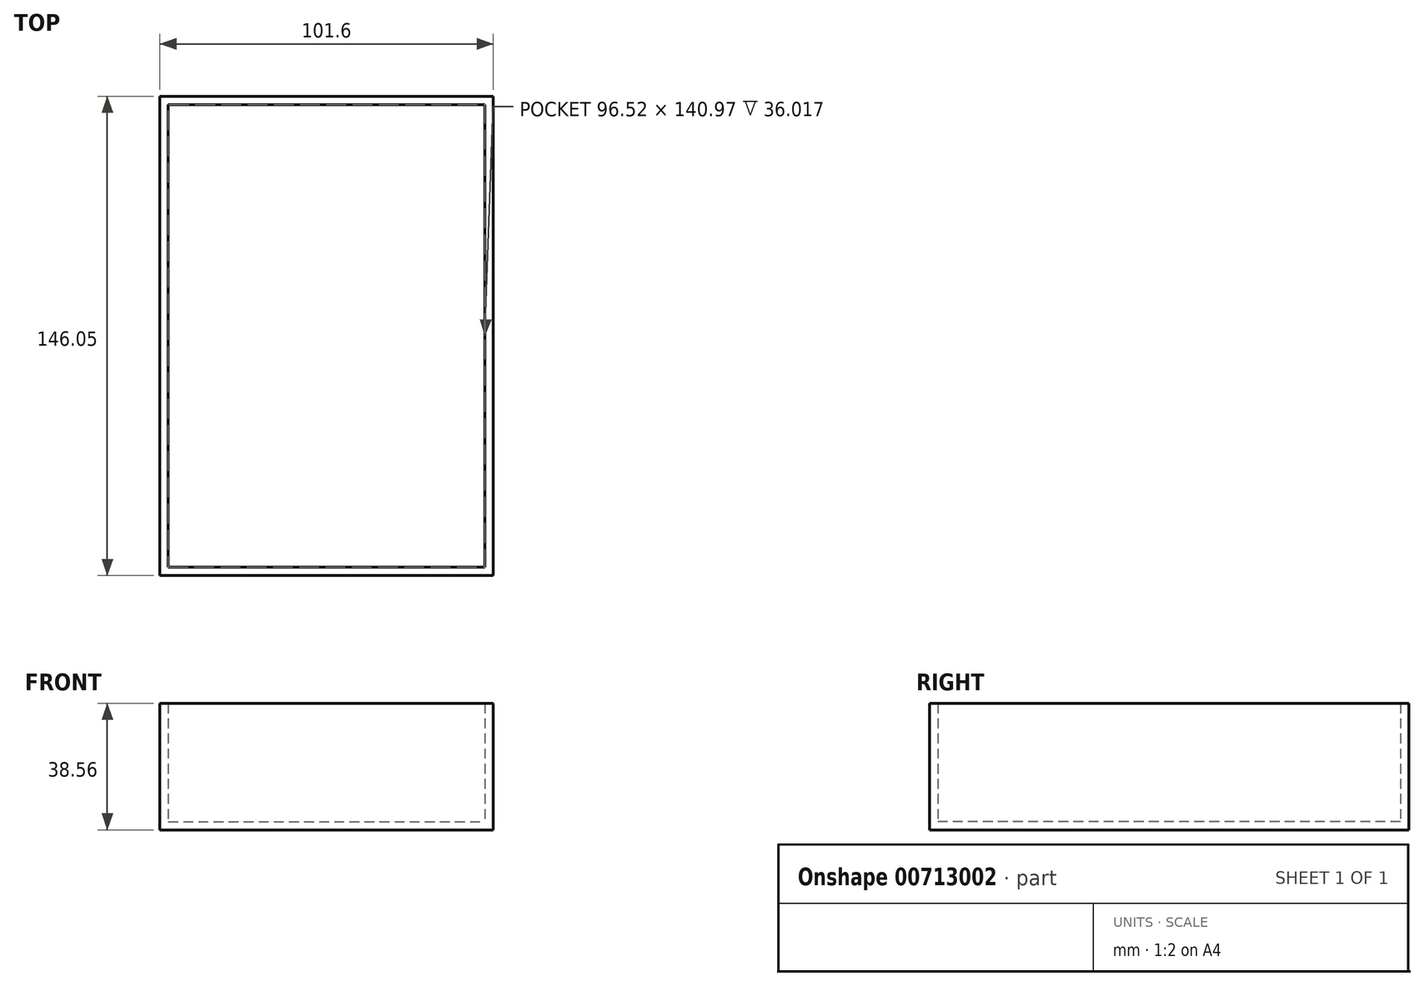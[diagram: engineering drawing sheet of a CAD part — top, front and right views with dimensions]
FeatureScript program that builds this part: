
annotation { "Feature Type Name" : "Feature", "Feature Type Description" : "" }
export const myFeature = defineFeature(function(context is Context, id is Id, definition is map)
    precondition{}
    {
        {
            var Q0;
            Q0=qCreatedBy(makeId("Top.planeOp"),FACE);
            var sketch = newSketch(context, id + "F0", { "sketchPlane" : qUnion([Q0])});
            skLineSegment(sketch, "E0.bottom", {"start": v(-59.18, 63.8) * mm, "end": v(42.42, 63.8) * mm});
            skLineSegment(sketch, "E0.top", {"start": v(-59.18, -82.24) * mm, "end": v(42.42, -82.24) * mm});
            skLineSegment(sketch, "E0.left", {"start": v(-59.18, 63.8) * mm, "end": v(-59.18, -82.24) * mm});
            skLineSegment(sketch, "E0.right", {"start": v(42.42, 63.8) * mm, "end": v(42.42, -82.24) * mm});
            skSolve(sketch);
        }
        {
            var Q0;
            Q0 = qSketchRegion(id + "F0", true);
            extrude(context, id + "F1", {"entities" : qUnion([Q0]), "depth" : 25.4 * mm, "offsetDistance" : 25.4 * mm});
        }
        {
            var Q0;
            Q0=makeQuery(id+"F1.opExtrude","CAP_FACE",FACE,{"disambiguationData":[OSD([sQuery(id+"F0.wireOp",EDGE,"E0.bottom"),sQuery(id+"F0.wireOp",EDGE,"E0.top"),sQuery(id+"F0.wireOp",EDGE,"E0.left"),sQuery(id+"F0.wireOp",EDGE,"E0.right")])],"isStart":false});
            shell(context, id + "F2", {"entities" : qUnion([Q0]), "thickness" : 2.54 * mm});
        }
        {
            var Q0;
            Q0=makeQuery(id+"F1.opExtrude","CAP_FACE",FACE,{"disambiguationData":[OSD([sQuery(id+"F0.wireOp",EDGE,"E0.bottom"),sQuery(id+"F0.wireOp",EDGE,"E0.top"),sQuery(id+"F0.wireOp",EDGE,"E0.left"),sQuery(id+"F0.wireOp",EDGE,"E0.right")])],"isStart":false});
            extrude(context, id + "F3", {"entities" : qUnion([Q0]), "operationType" : NewBodyOperationType.ADD, "depth" : 13.16 * mm, "offsetDistance" : 25.4 * mm});
        }
    });
